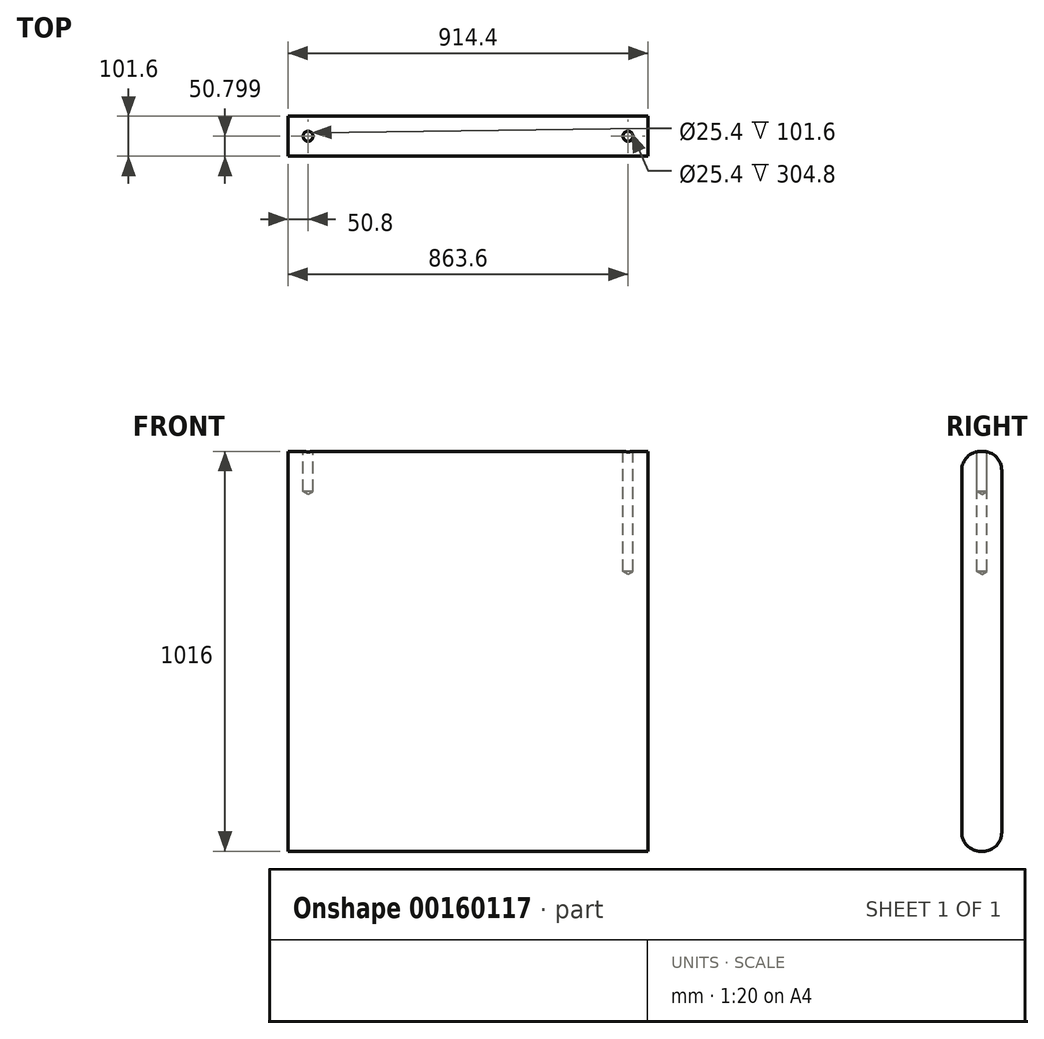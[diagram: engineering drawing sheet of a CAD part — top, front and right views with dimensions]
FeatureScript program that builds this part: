
annotation { "Feature Type Name" : "Feature", "Feature Type Description" : "" }
export const myFeature = defineFeature(function(context is Context, id is Id, definition is map)
    precondition{}
    {
        {
            var Q0;
            Q0=qCreatedBy(makeId("Right.planeOp"),FACE);
            var sketch = newSketch(context, id + "F0", { "sketchPlane" : qUnion([Q0])});
            skLineSegment(sketch, "E0.bottom", {"start": v(1.23, 1012.44) * mm, "end": v(6.3, 1012.44) * mm});
            skLineSegment(sketch, "E0.top", {"start": v(1.23, -3.56) * mm, "end": v(6.3, -3.56) * mm});
            skLineSegment(sketch, "E0.left", {"start": v(-47.03, 964.18) * mm, "end": v(-47.03, 44.7) * mm});
            skLineSegment(sketch, "E0.right", {"start": v(54.57, 964.18) * mm, "end": v(54.57, 44.7) * mm});
            skPoint(sketch, "E1.visualSharp", {"position": v(-47.03, 1012.44) * mm});
            skArc(sketch, "E1.filletArc", {"start": v(1.23, 1012.44) * mm, "mid": v(-32.9, 998.3) * mm, "end": v(-47.03, 964.18) * mm});
            skPoint(sketch, "E2.visualSharp", {"position": v(54.57, 1012.44) * mm});
            skArc(sketch, "E2.filletArc", {"start": v(54.57, 964.18) * mm, "mid": v(40.43, 998.3) * mm, "end": v(6.3, 1012.44) * mm});
            skPoint(sketch, "E3.visualSharp", {"position": v(-47.03, -3.56) * mm});
            skArc(sketch, "E3.filletArc", {"start": v(-47.03, 44.7) * mm, "mid": v(-32.9, 10.57) * mm, "end": v(1.23, -3.56) * mm});
            skPoint(sketch, "E4.visualSharp", {"position": v(54.57, -3.56) * mm});
            skArc(sketch, "E4.filletArc", {"start": v(6.3, -3.56) * mm, "mid": v(40.43, 10.57) * mm, "end": v(54.57, 44.7) * mm});
            skSolve(sketch);
        }
        {
            var Q0;
            Q0=makeQuery(id+"F0.imprint","IMPRINT",FACE,{"disambiguationData":[TD([[makeQuery(id+"F0.imprint","IMPRINT",EDGE,{"derivedFrom":sQuery(id+"F0.wireOp",EDGE,"E0.left")}),1.0]])]});
            extrude(context, id + "F1", {"entities" : qUnion([Q0]), "depth" : 914.4 * mm});
        }
        {
            var Q0;
            Q0=makeQuery(id+"F1.opExtrude","SWEPT_FACE",FACE,{"disambiguationData":[OSD([sQuery(id+"F0.wireOp",EDGE,"E0.bottom")])]});
            var sketch = newSketch(context, id + "F2", { "sketchPlane" : qUnion([Q0])});
            skLineSegment(sketch, "E5", {"start": v(0, 3.77) * mm, "end": v(50.8, 3.77) * mm});
            skLineSegment(sketch, "E6", {"start": v(914.4, 3.77) * mm, "end": v(863.6, 3.77) * mm});
            skSolve(sketch);
        }
        {
            var Q0;
            Q0=sQuery(id+"F2.wireOp",VERTEX,"E5.end");
            var Q1;
            Q1=makeQuery(id+"F1.opExtrude","SWEPT_BODY",BODY,{"disambiguationData":[OSD([sQuery(id+"F0.wireOp",EDGE,"E0.bottom"),sQuery(id+"F0.wireOp",EDGE,"E0.top"),sQuery(id+"F0.wireOp",EDGE,"E0.left"),sQuery(id+"F0.wireOp",EDGE,"E0.right"),sQuery(id+"F0.wireOp",EDGE,"E1.filletArc"),sQuery(id+"F0.wireOp",EDGE,"E2.filletArc"),sQuery(id+"F0.wireOp",EDGE,"E3.filletArc"),sQuery(id+"F0.wireOp",EDGE,"E4.filletArc")])]});
            hole(context, id + "F3", {"style" : HoleStyle.SIMPLE, "endStyle" : HoleEndStyle.BLIND, "holeDiameter" : 25.4 * mm, "holeDepth" : 101.6 * mm, "startFromSketch" : true, "locations" : qUnion([Q0]), "scope" : qUnion([Q1])});
        }
        {
            var Q0;
            Q0=sQuery(id+"F2.wireOp",VERTEX,"E6.end");
            var Q1;
            Q1=makeQuery(id+"F1.opExtrude","SWEPT_BODY",BODY,{"disambiguationData":[OSD([sQuery(id+"F0.wireOp",EDGE,"E0.bottom"),sQuery(id+"F0.wireOp",EDGE,"E0.top"),sQuery(id+"F0.wireOp",EDGE,"E0.left"),sQuery(id+"F0.wireOp",EDGE,"E0.right"),sQuery(id+"F0.wireOp",EDGE,"E1.filletArc"),sQuery(id+"F0.wireOp",EDGE,"E2.filletArc"),sQuery(id+"F0.wireOp",EDGE,"E3.filletArc"),sQuery(id+"F0.wireOp",EDGE,"E4.filletArc")])]});
            hole(context, id + "F4", {"style" : HoleStyle.SIMPLE, "endStyle" : HoleEndStyle.BLIND, "holeDiameter" : 25.4 * mm, "holeDepth" : 304.8 * mm, "startFromSketch" : true, "locations" : qUnion([Q0]), "scope" : qUnion([Q1])});
        }
    });
